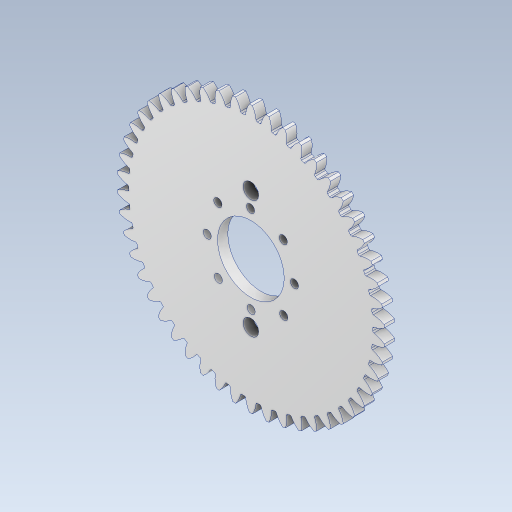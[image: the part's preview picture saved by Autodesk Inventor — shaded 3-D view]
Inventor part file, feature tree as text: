
AUTODESK INVENTOR PART (.ipt)
format: ipt  version: 2023.1 (Build 271208000, 208)  size: 1,029,120 bytes
history: native  units: mm
features: extrude x9, sketch x9, projected_geometry x5, other x4, reference x2, pattern_circular x1
ambient origin geometry x8: Origin, YZ Plane, XZ Plane, XY Plane, X Axis, Y Axis, Z Axis, Center Point
bodies: Body1 (feature_tree)
feature tree (30):
  other  "솔리드1"
  extrude  "돌출1"  Depth=4.0mm TaperAngle=0.0deg
  pattern_circular  "원형 패턴1"  Count=50 Angle=360.0deg
  extrude  "돌출3"  TaperAngle=0.0deg  [1 undecoded]
  extrude  "돌출4"  Depth=6.1mm
  extrude  "돌출5"  Depth=6.1mm
  extrude  "돌출6"  Depth=35.0mm
  extrude  "돌출7"  Depth=35.0mm
  extrude  "돌출8"  Depth=10.0mm TaperAngle=0.0deg
  extrude  "돌출9"  Depth=10.0mm TaperAngle=0.0deg
  extrude  "돌출10"  Depth=45.0mm
  sketch  "스케치1"
  sketch  "스케치3"
  sketch  "스케치4"
  sketch  "스케치5"
  projected_geometry  "투영된 루프1"
  sketch  "스케치6"
  projected_geometry  "투영된 루프2"
  sketch  "스케치7"
  projected_geometry  "투영된 루프3"
  sketch  "스케치10"
  reference  "참조3"
  reference  "참조4"
  sketch  "스케치11"
  sketch  "스케치12"
  projected_geometry  "투영된 루프4"
  projected_geometry  "투영된 루프5"
  other  "<userpath>\Desktop\2022 manipulator (국방로봇)\JWM.iam"
  other  "JWM.iam"
  other  "큰모터아이들러:8"
note: 1 required parameter value undecoded (feature->parameter linkage not recoverable at this tier; creation-order binding heuristic only, values carry confidence <= 0.55)
